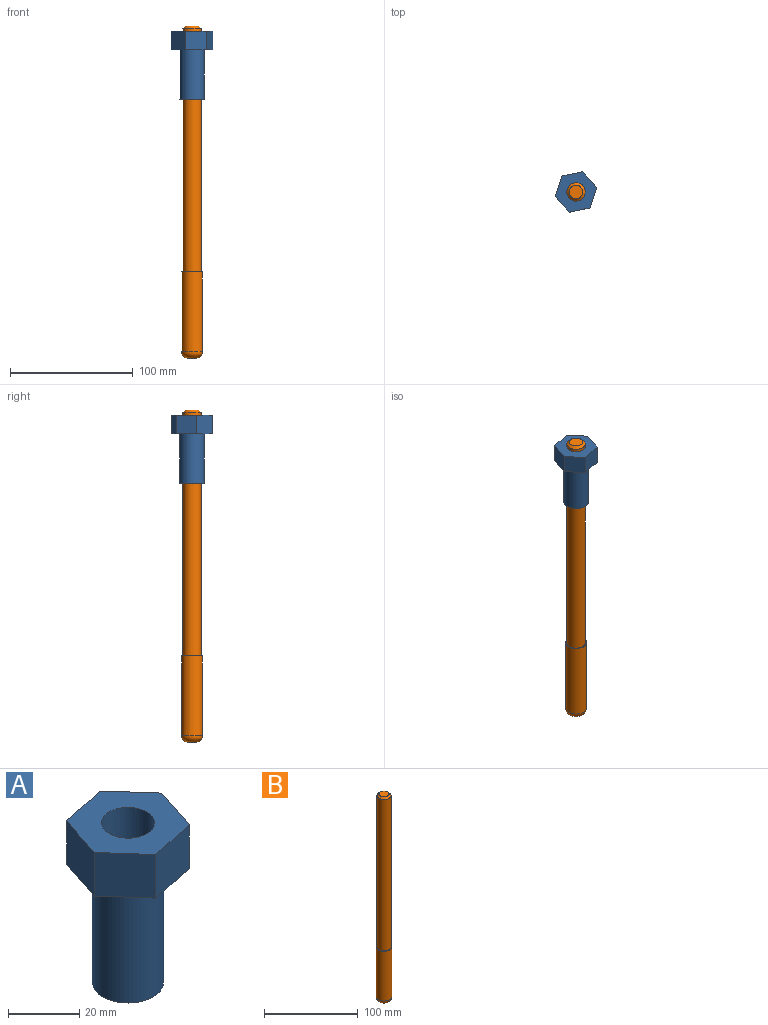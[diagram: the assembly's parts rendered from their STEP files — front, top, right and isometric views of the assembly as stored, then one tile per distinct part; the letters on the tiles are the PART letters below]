
ASSEMBLY  parts=2 mates=1
PART A: 12 faces, bbox 33.9x32.9x55 mm
  f0: cylinder r=10mm len=40mm, axis (0,0,-1), area 2513.3mm2, adj f1,f9
  f1: plane 20x20mm, normal (0,0,-1), area 87.2mm2, adj f0,f11
  f2: plane 15x12.94mm, normal (0.75,0.66,0), area 259.8mm2, adj f3,f7,f8,f9
  f3: plane 16.96x15mm, normal (-0.2,0.98,0), area 259.8mm2, adj f2,f4,f8,f9
  f4: plane 16.44x15mm, normal (-0.95,0.31,0), area 259.8mm2, adj f3,f5,f8,f9
  f5: plane 15x12.94mm, normal (-0.75,-0.66,0), area 259.8mm2, adj f4,f6,f8,f9
  f6: plane 16.96x15mm, normal (0.2,-0.98,0), area 259.8mm2, adj f5,f7,f8,f9
  f7: plane 16.44x15mm, normal (0.95,-0.31,0), area 259.8mm2, adj f2,f6,f8,f9
  f8: plane 33.93x32.88mm, normal (0,0,1), area 602.7mm2, adj f2,f3,f4,f5,f6,f7,f10
  f9: plane 33.93x32.88mm, normal (0,0,-1), area 465.3mm2, adj f0,f2,f3,f4,f5,f6,f7
  f10: cylinder r=7.5mm len=54mm, axis (0,0,1), area 2544.7mm2, adj f8,f11
  f11: cone r=8.5mm half-angle=45deg, axis (0,0,-1), area 71.1mm2, adj f1,f10
PART B: 7 faces, bbox 17x17x270 mm
  f0: cylinder r=8.5mm len=65mm, axis (0,0,-1), area 3471.5mm2, adj f1,f5
  f1: plane 17x17mm, normal (0,0,1), area 50.3mm2, adj f0,f3
  f2: plane 7x7mm, normal (0,0,-1), area 38.5mm2, adj f5
  f3: cylinder r=7.5mm len=198mm, axis (0,0,-1), area 9330.5mm2, adj f1,f6
  f4: plane 11x11mm, normal (0,0,1), area 95mm2, adj f6
  f5: torus R=3.5mm, axis (0,0,1), area 329.8mm2, adj f0,f2
  f6: cone r=5.5mm half-angle=45deg, axis (0,0,-1), area 115.5mm2, adj f3,f4
PLACE A t=(-93.59,-42.16,238.68)mm
PLACE B t=(-93.59,-42.16,28.12)mm
MATE slider B.f3 <-> A.f10  axis (0,0,1) through (-93.59,-42.16,298.12)mm
